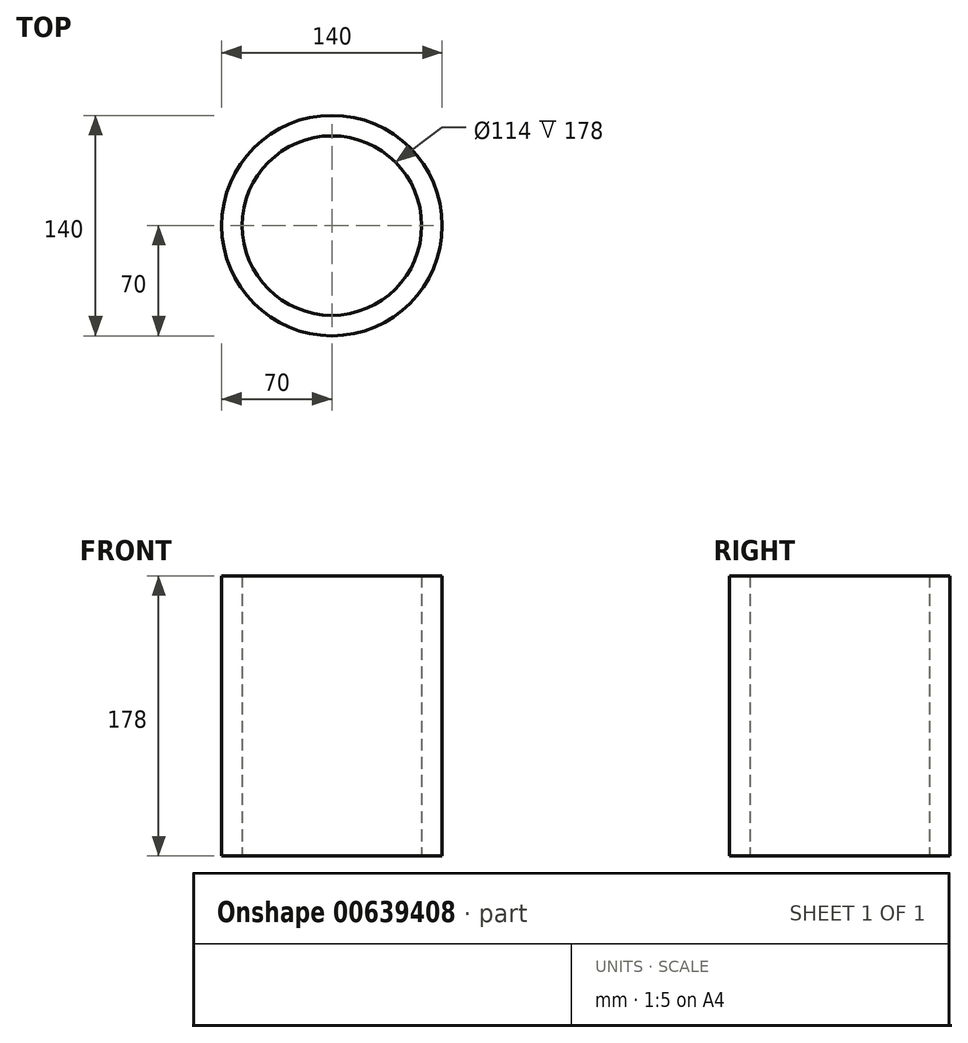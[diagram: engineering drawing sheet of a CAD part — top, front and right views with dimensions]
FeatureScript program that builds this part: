
annotation { "Feature Type Name" : "Feature", "Feature Type Description" : "" }
export const myFeature = defineFeature(function(context is Context, id is Id, definition is map)
    precondition{}
    {
        {
            var Q0;
            Q0=qCreatedBy(makeId("Top.planeOp"),FACE);
            var sketch = newSketch(context, id + "F0", { "sketchPlane" : qUnion([Q0])});
            skCircle(sketch, "E0", {"center": v(0, 0) * mm, "radius": 70 * mm});
            skCircle(sketch, "E1", {"center": v(0, 0) * mm, "radius": 57 * mm});
            skSolve(sketch);
        }
        {
            var Q0;
            Q0=makeQuery(id+"F0.imprint","IMPRINT",FACE,{"disambiguationData":[TD([[makeQuery(id+"F0.imprint","IMPRINT",EDGE,{"derivedFrom":sQuery(id+"F0.wireOp",EDGE,"E0")}),1.0]])]});
            extrude(context, id + "F1", {"entities" : qUnion([Q0]), "depth" : 178 * mm, "offsetDistance" : 25 * mm});
        }
    });
